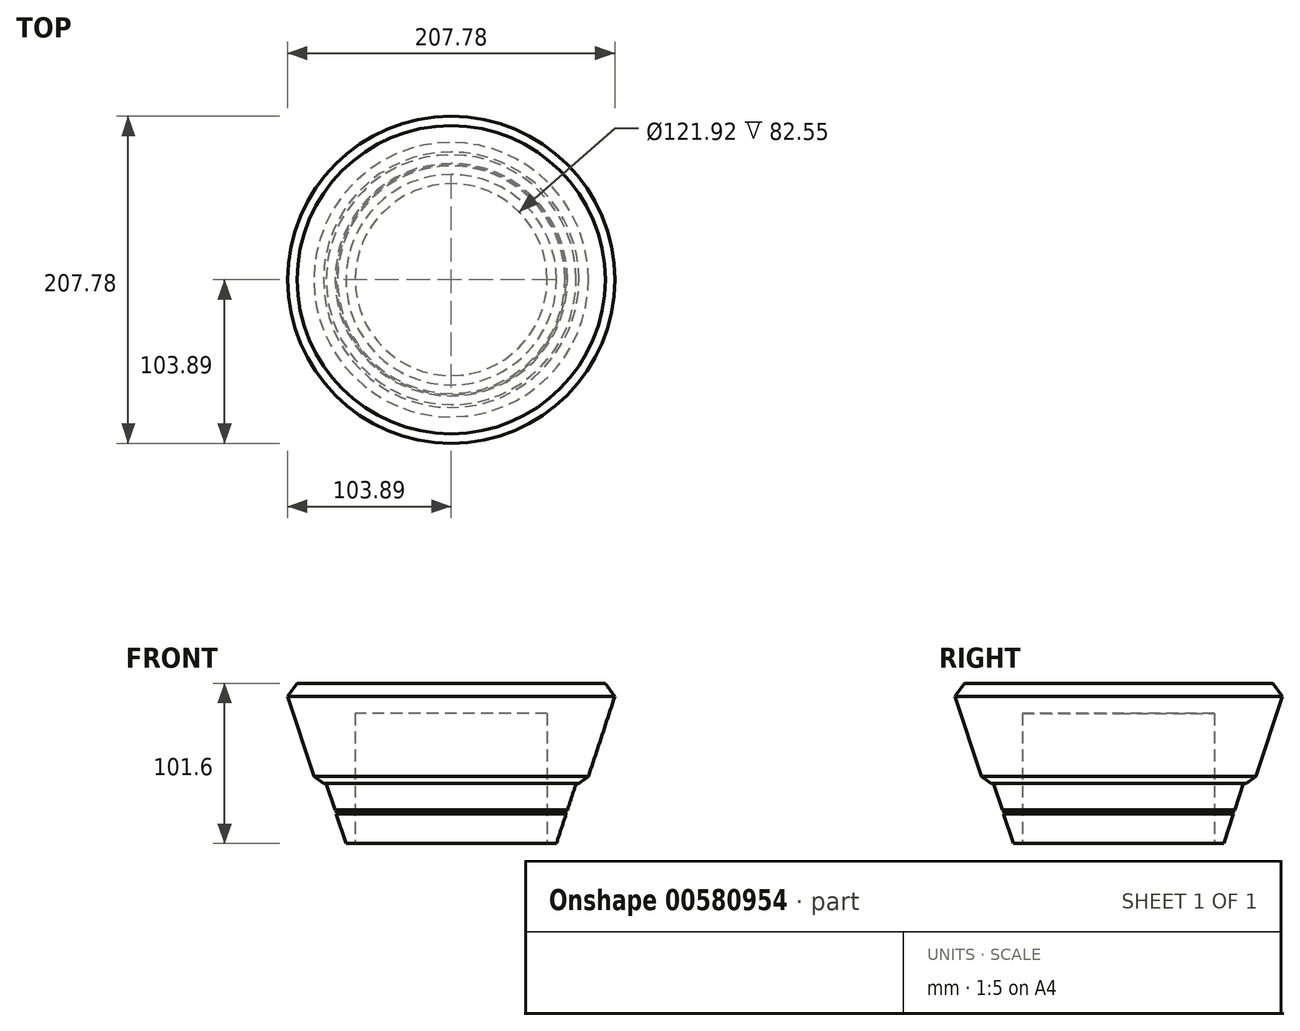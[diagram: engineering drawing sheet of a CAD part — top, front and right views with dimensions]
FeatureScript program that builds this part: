
annotation { "Feature Type Name" : "Feature", "Feature Type Description" : "" }
export const myFeature = defineFeature(function(context is Context, id is Id, definition is map)
    precondition{}
    {
        {
            var Q0;
            Q0=qCreatedBy(makeId("Top.planeOp"),FACE);
            var sketch = newSketch(context, id + "F0", { "sketchPlane" : qUnion([Q0])});
            skCircle(sketch, "E0", {"center": v(0, 0) * mm, "radius": 66.85 * mm});
            skSolve(sketch);
        }
        {
            var Q0;
            Q0=qCreatedBy(makeId("Top.planeOp"),FACE);
            cPlane(context, id + "F1", {"entities" : qUnion([Q0]), "cplaneType" : CPlaneType.OFFSET, "offset" : 101.6 * mm, "width" : 152.4 * mm, "height" : 152.4 * mm});
        }
        {
            var Q0;
            Q0=qCreatedBy(id+"F1.planeOp",FACE);
            var sketch = newSketch(context, id + "F2", { "sketchPlane" : qUnion([Q0])});
            skCircle(sketch, "E1", {"center": v(0, 0) * mm, "radius": 100.28 * mm});
            skSolve(sketch);
        }
        {
            var Q0;
            Q0=makeQuery(id+"F2.imprint","IMPRINT",FACE,{"disambiguationData":[TD([[makeQuery(id+"F2.imprint","IMPRINT",EDGE,{"derivedFrom":sQuery(id+"F2.wireOp",EDGE,"E1")}),1.0]])]});
            var Q1;
            Q1=makeQuery(id+"F0.imprint","IMPRINT",FACE,{"disambiguationData":[TD([[makeQuery(id+"F0.imprint","IMPRINT",EDGE,{"derivedFrom":sQuery(id+"F0.wireOp",EDGE,"E0")}),1.0]])]});
            var Q2;
            Q2=sQuery(id+"F2.wireOp",EDGE,"Eyu8YDiN-lEGU-Wuxt-0ncA-RZLAWeJK4OgB");
            var Q3;
            Q3=sQuery(id+"F0.wireOp",EDGE,"fgfE4CqQ-t5n6-ucAx-yhIW-5wF2yx0Jya2k");
            loft(context, id + "F3", {"sheetProfilesArray" : [{ "sheetProfileEntities" : qUnion([Q0]) }, { "sheetProfileEntities" : qUnion([Q1]) }], "wireProfilesArray" : [{ "wireProfileEntities" : qUnion([Q2]) }, { "wireProfileEntities" : qUnion([Q3]) }]});
        }
        {
            var Q0;
            Q0=qCreatedBy(makeId("Top.planeOp"),FACE);
            var sketch = newSketch(context, id + "F4", { "sketchPlane" : qUnion([Q0])});
            skCircle(sketch, "E2", {"center": v(0, 0) * mm, "radius": 60.96 * mm});
            skSolve(sketch);
        }
        {
            var Q0;
            Q0=qCreatedBy(makeId("Top.planeOp"),FACE);
            cPlane(context, id + "F5", {"entities" : qUnion([Q0]), "cplaneType" : CPlaneType.OFFSET, "offset" : 38.1 * mm, "width" : 152.4 * mm, "height" : 152.4 * mm});
        }
        {
            var Q0;
            Q0=qCreatedBy(id+"F5.planeOp",FACE);
            var sketch = newSketch(context, id + "F6", { "sketchPlane" : qUnion([Q0])});
            skCircle(sketch, "E3", {"center": v(0, 0) * mm, "radius": 85.73 * mm});
            skSolve(sketch);
        }
        {
            var Q0;
            Q0=qCreatedBy(id+"F1.planeOp",FACE);
            var sketch = newSketch(context, id + "F7", { "sketchPlane" : qUnion([Q0])});
            skCircle(sketch, "E4", {"center": v(0, 0) * mm, "radius": 106.63 * mm});
            skSolve(sketch);
        }
        {
            var Q1;
            Q1=makeQuery(id+"F6.imprint","IMPRINT",FACE,{"disambiguationData":[TD([[makeQuery(id+"F6.imprint","IMPRINT",EDGE,{"derivedFrom":sQuery(id+"F6.wireOp",EDGE,"E3")}),1.0]])]});
            var Q2;
            Q2=makeQuery(id+"F7.imprint","IMPRINT",FACE,{"disambiguationData":[TD([[makeQuery(id+"F7.imprint","IMPRINT",EDGE,{"derivedFrom":sQuery(id+"F7.wireOp",EDGE,"E4")}),1.0]])]});
            loft(context, id + "F8", {"operationType" : NewBodyOperationType.ADD, "sheetProfilesArray" : [{ "sheetProfileEntities" : qUnion([Q1]) }, { "sheetProfileEntities" : qUnion([Q2]) }]});
        }
        {
            var Q0;
            Q0=makeQuery(id+"F4.imprint","IMPRINT",FACE,{"disambiguationData":[TD([[makeQuery(id+"F4.imprint","IMPRINT",EDGE,{"derivedFrom":sQuery(id+"F4.wireOp",EDGE,"E2")}),1.0]])]});
            extrude(context, id + "F9", {"entities" : qUnion([Q0]), "operationType" : NewBodyOperationType.REMOVE, "endBound" : BoundingType.UP_TO_NEXT, "depth" : 62.23 * mm, "hasOffset" : true, "offsetDistance" : 19.05 * mm});
        }
        {
            var Q0;
            Q0=makeQuery(id+"F8.opLoft","MID_CAP_EDGE",EDGE,{"disambiguationData":[OSD([sQuery(id+"F6.wireOp",EDGE,"E3")])],"capPos":0.0});
            chamfer(context, id + "F10", {"entities" : qUnion([Q0]), "width" : 6.35 * mm, "tangentPropagation" : true});
        }
        {
            var Q0;
            Q0=makeQuery(id+"F8.opLoft","MID_CAP_EDGE",EDGE,{"disambiguationData":[OSD([sQuery(id+"F6.wireOp",EDGE,"E3"),sQuery(id+"F7.wireOp",EDGE,"E4")])],"capPos":1.0});
            chamfer(context, id + "F11", {"entities" : qUnion([Q0]), "width" : 6.35 * mm, "tangentPropagation" : true});
        }
        {
            var Q0;
            Q0=qCreatedBy(makeId("Front.planeOp"),FACE);
            var sketch = newSketch(context, id + "F12", { "sketchPlane" : qUnion([Q0])});
            skLineSegment(sketch, "E5", {"start": v(-79.4, 38.11) * mm, "end": v(-66.85, 0) * mm});
            skLineSegment(sketch, "E6", {"start": v(-73.8, 21.14) * mm, "end": v(-72.2, 20.33) * mm});
            skLineSegment(sketch, "E7", {"start": v(-72.2, 20.33) * mm, "end": v(-73.02, 18.73) * mm});
            skSolve(sketch);
        }
        {
            var Q0;
            Q0=qCreatedBy(makeId("Right.planeOp"),FACE);
            var sketch = newSketch(context, id + "F13", { "sketchPlane" : qUnion([Q0])});
            skLineSegment(sketch, "E8", {"start": v(0, 0) * mm, "end": v(0, 184.2) * mm});
            skSolve(sketch);
        }
        {
            var Q0;
            Q0 = qSketchRegion(id + "F12", true);
            var Q1;
            Q1=sQuery(id+"F13.wireOp",EDGE,"E8");
            revolve(context, id + "F14", {"operationType" : NewBodyOperationType.REMOVE, "entities" : qUnion([Q0]), "axis" : qUnion([Q1]), "revolveType" : RevolveType.FULL, "oppositeDirection" : true});
        }
    });
